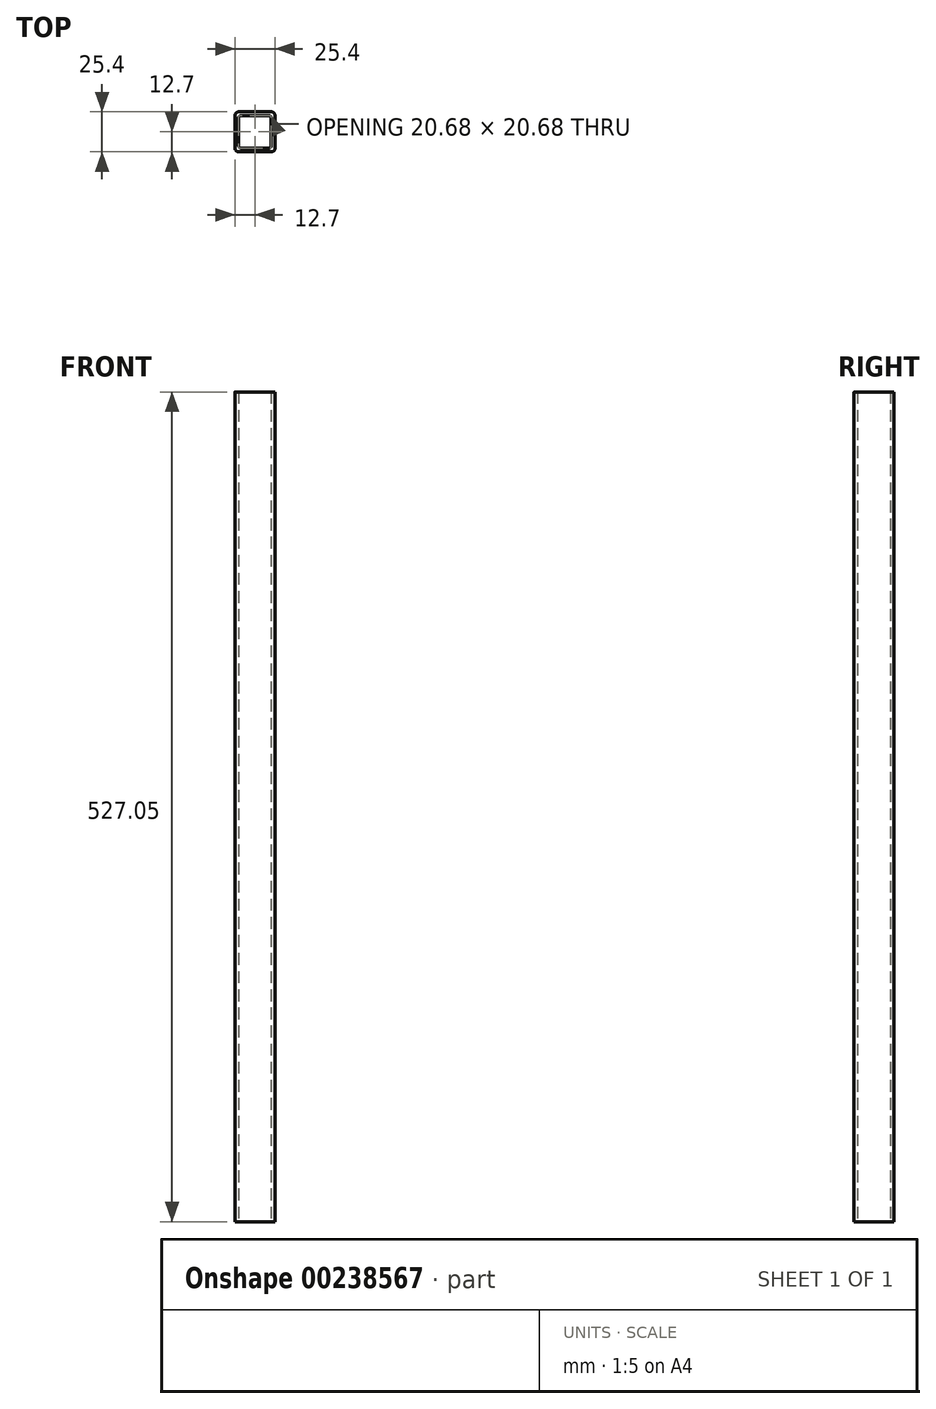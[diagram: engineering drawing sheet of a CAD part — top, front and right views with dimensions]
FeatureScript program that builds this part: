
annotation { "Feature Type Name" : "Feature", "Feature Type Description" : "" }
export const myFeature = defineFeature(function(context is Context, id is Id, definition is map)
    precondition{}
    {
        {
            var Q0;
            Q0=qCreatedBy(makeId("Top.planeOp"),FACE);
            var sketch = newSketch(context, id + "F0", { "sketchPlane" : qUnion([Q0])});
            skLineSegment(sketch, "E0", {"start": v(-12.7, 10.34) * mm, "end": v(-12.7, -10.34) * mm});
            skLineSegment(sketch, "E1", {"start": v(-10.34, -12.7) * mm, "end": v(10.34, -12.7) * mm});
            skLineSegment(sketch, "E2", {"start": v(12.7, -10.34) * mm, "end": v(12.7, 10.34) * mm});
            skLineSegment(sketch, "E3", {"start": v(10.34, 12.7) * mm, "end": v(-10.34, 12.7) * mm});
            skLineSegment(sketch, "E4", {"start": v(0, 12.7) * mm, "end": v(0, -12.7) * mm, "construction": true});
            skLineSegment(sketch, "E5", {"start": v(-12.7, 0) * mm, "end": v(12.7, 0) * mm, "construction": true});
            skPoint(sketch, "E6", {"position": v(0, 0) * mm});
            skPoint(sketch, "E7.visualSharp", {"position": v(-12.7, 12.7) * mm});
            skArc(sketch, "E7.filletArc", {"start": v(-10.34, 12.7) * mm, "mid": v(-12, 12) * mm, "end": v(-12.7, 10.34) * mm});
            skPoint(sketch, "E8.visualSharp", {"position": v(12.7, 12.7) * mm});
            skArc(sketch, "E8.filletArc", {"start": v(12.7, 10.34) * mm, "mid": v(12, 12) * mm, "end": v(10.34, 12.7) * mm});
            skPoint(sketch, "E9.visualSharp", {"position": v(12.7, -12.7) * mm});
            skArc(sketch, "E9.filletArc", {"start": v(10.34, -12.7) * mm, "mid": v(12, -12) * mm, "end": v(12.7, -10.34) * mm});
            skPoint(sketch, "E10.visualSharp", {"position": v(-12.7, -12.7) * mm});
            skArc(sketch, "E10.filletArc", {"start": v(-12.7, -10.34) * mm, "mid": v(-12, -12) * mm, "end": v(-10.34, -12.7) * mm});
            skLineSegment(sketch, "E11.0", {"start": v(8.81, 10.34) * mm, "end": v(-8.81, 10.34) * mm});
            skLineSegment(sketch, "E12.0", {"start": v(10.34, -8.81) * mm, "end": v(10.34, 8.81) * mm});
            skLineSegment(sketch, "E13.0", {"start": v(-8.81, -10.34) * mm, "end": v(8.81, -10.34) * mm});
            skLineSegment(sketch, "E14.0", {"start": v(-10.34, 8.81) * mm, "end": v(-10.34, -8.81) * mm});
            skArc(sketch, "E15.filletArc", {"start": v(-8.81, 10.34) * mm, "mid": v(-9.9, 9.9) * mm, "end": v(-10.34, 8.81) * mm});
            skArc(sketch, "E16.filletArc", {"start": v(10.34, 8.81) * mm, "mid": v(9.9, 9.9) * mm, "end": v(8.81, 10.34) * mm});
            skArc(sketch, "E17.filletArc", {"start": v(8.81, -10.34) * mm, "mid": v(9.9, -9.9) * mm, "end": v(10.34, -8.81) * mm});
            skArc(sketch, "E18.filletArc", {"start": v(-10.34, -8.81) * mm, "mid": v(-9.9, -9.9) * mm, "end": v(-8.81, -10.34) * mm});
            skSolve(sketch);
        }
        {
            var Q0;
            Q0=makeQuery(id+"F0.imprint","IMPRINT",FACE,{"disambiguationData":[TD([[makeQuery(id+"F0.imprint","IMPRINT",EDGE,{"derivedFrom":sQuery(id+"F0.wireOp",EDGE,"E0")}),1.0]])]});
            extrude(context, id + "F1", {"entities" : qUnion([Q0]), "depth" : 527.05 * mm});
        }
    });
